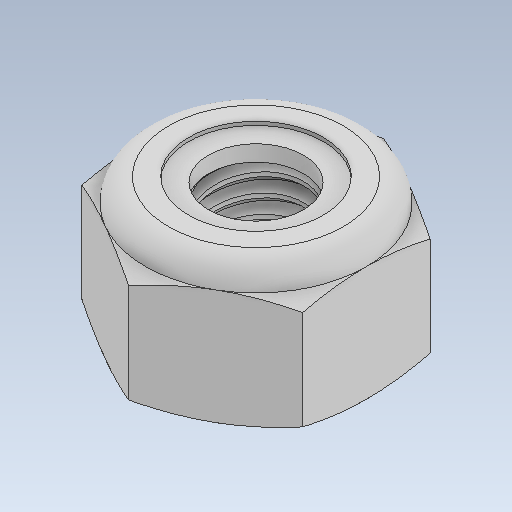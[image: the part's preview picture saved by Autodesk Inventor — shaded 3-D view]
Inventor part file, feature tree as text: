
AUTODESK INVENTOR PART (.ipt)
format: ipt  version: 2023 (Build 270158000, 158)  size: 288,768 bytes
history: native  units: in
note: dims shown in document units (in); Inventor stores cm internally (conversion verified against a paired STEP export)
features: other x1, revolve x1
ambient origin geometry x8: Origin, YZ Plane, XZ Plane, XY Plane, X Axis, Y Axis, Z Axis, Center Point
bodies: Solid1 (feature_tree), Solid2 (feature_tree)
feature tree (2):
  other  "Cut-Revolve4"
  revolve  "Revolve2"  [1 undecoded]
note: 1 required parameter value undecoded (feature->parameter linkage not recoverable at this tier; creation-order binding heuristic only, values carry confidence <= 0.55)
